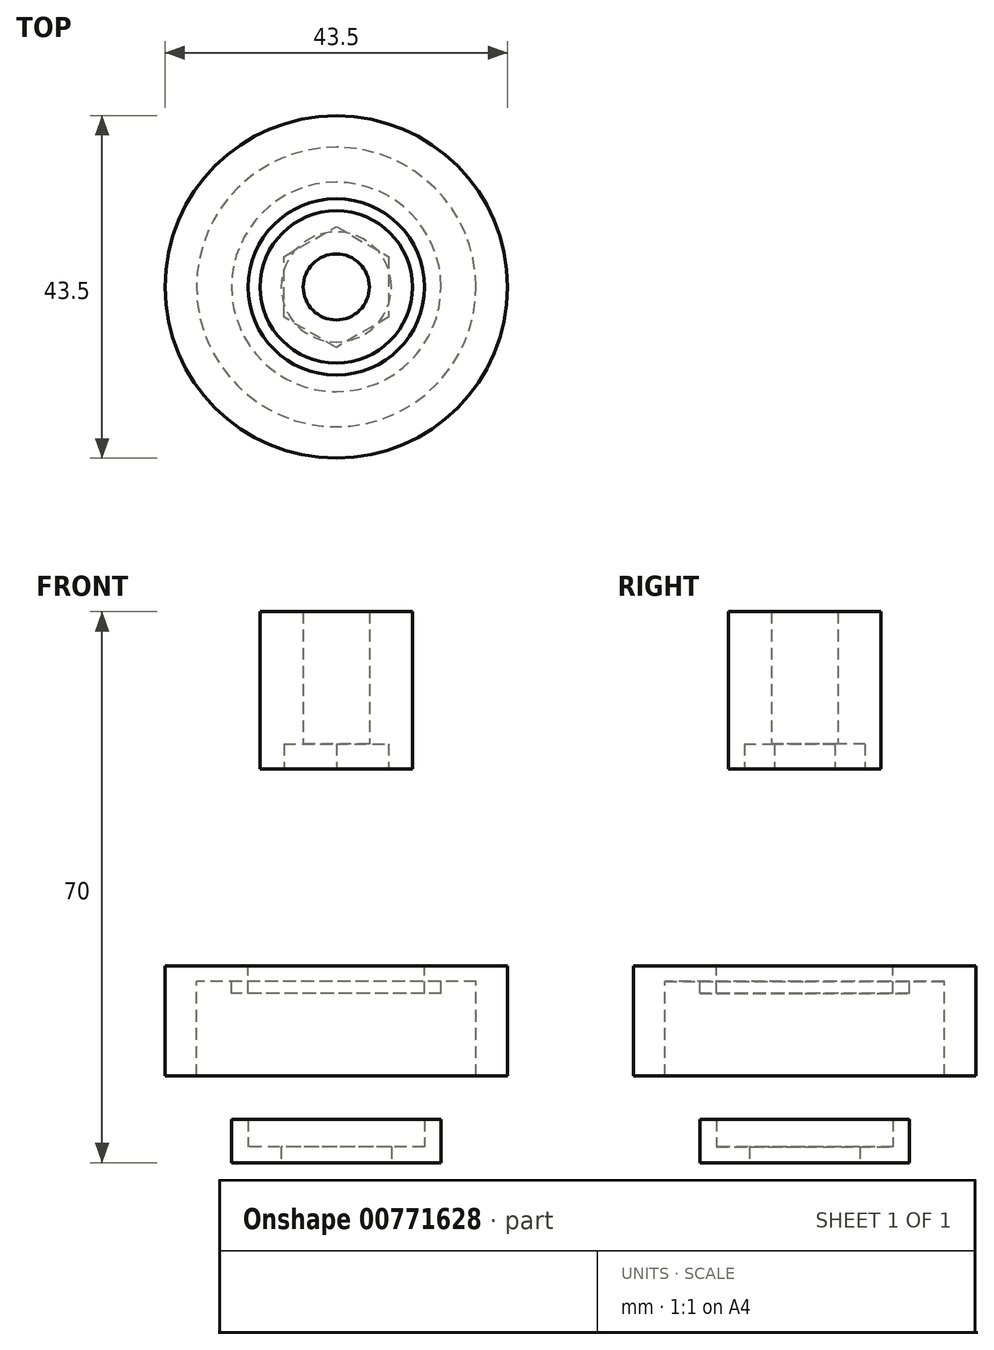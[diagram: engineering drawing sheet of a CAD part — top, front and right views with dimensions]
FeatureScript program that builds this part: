
annotation { "Feature Type Name" : "Feature", "Feature Type Description" : "" }
export const myFeature = defineFeature(function(context is Context, id is Id, definition is map)
    precondition{}
    {
        {
            assignVariable(context, id + "F0", {"variableType" : VariableType.LENGTH, "name" : "Bearing_T", "lengthValue" : 7 * mm});
        }
        {
            assignVariable(context, id + "F1", {"variableType" : VariableType.LENGTH, "name" : "Min_Wall_T", "lengthValue" : 2 * mm});
        }
        {
            assignVariable(context, id + "F2", {"variableType" : VariableType.LENGTH, "name" : "M8_Nut_T", "lengthValue" : (0.8 * 8) * mm});
        }
        {
            assignVariable(context, id + "F3", {"variableType" : VariableType.LENGTH, "name" : "Spacer_L", "lengthValue" : 20 * mm});
        }
        {
            var Q0;
            Q0=qCreatedBy(makeId("Top.planeOp"),FACE);
            var sketch = newSketch(context, id + "F4", { "sketchPlane" : qUnion([Q0])});
            skCircle(sketch, "E0", {"center": v(0, 0) * mm, "radius": 7 * mm});
            skCircle(sketch, "E1", {"center": v(0, 0) * mm, "radius": 13.3 * mm});
            skCircle(sketch, "E2", {"center": v(0, 0) * mm, "radius": 11.2 * mm});
            skSolve(sketch);
        }
        {
            var Q0;
            Q0=makeQuery(id+"F4.imprint","IMPRINT",FACE,{"disambiguationData":[TD([[makeQuery(id+"F4.imprint","IMPRINT",EDGE,{"derivedFrom":sQuery(id+"F4.wireOp",EDGE,"E0")}),-1.0]])]});
            var Q1;
            Q1=makeQuery(id+"F4.imprint","IMPRINT",FACE,{"disambiguationData":[TD([[makeQuery(id+"F4.imprint","IMPRINT",EDGE,{"derivedFrom":sQuery(id+"F4.wireOp",EDGE,"E1")}),1.0]])]});
            extrude(context, id + "F5", {"entities" : qUnion([Q0, Q1]), "depth" : getVariable(context, 'Min_Wall_T'), "offsetDistance" : 25 * mm});
        }
        {
            var Q0;
            Q0=makeQuery(id+"F4.imprint","IMPRINT",FACE,{"disambiguationData":[TD([[makeQuery(id+"F4.imprint","IMPRINT",EDGE,{"derivedFrom":sQuery(id+"F4.wireOp",EDGE,"E1")}),1.0]])]});
            extrude(context, id + "F6", {"entities" : qUnion([Q0]), "operationType" : NewBodyOperationType.ADD, "depth" : (getVariable(context, 'Bearing_T') / 2) + getVariable(context, 'Min_Wall_T'), "offsetDistance" : 25 * mm});
        }
        {
            var Q0;
            Q0=qCreatedBy(makeId("Top.planeOp"),FACE);
            cPlane(context, id + "F7", {"entities" : qUnion([Q0]), "cplaneType" : CPlaneType.OFFSET, "offset" : 25 * mm, "width" : 150 * mm, "height" : 150 * mm});
        }
        {
            var Q0;
            Q0=qCreatedBy(id+"F7.planeOp",FACE);
            var sketch = newSketch(context, id + "F8", { "sketchPlane" : qUnion([Q0])});
            skCircle(sketch, "E3", {"center": v(0, 0) * mm, "radius": 17.75 * mm});
            skCircle(sketch, "E4.0", {"center": v(0, 0) * mm, "radius": 21.75 * mm});
            skCircle(sketch, "E5.0", {"center": v(0, 0) * mm, "radius": 13.3 * mm});
            skCircle(sketch, "E6.0", {"center": v(0, 0) * mm, "radius": 11.2 * mm});
            skSolve(sketch);
        }
        {
            var Q0;
            Q0=makeQuery(id+"F8.imprint","IMPRINT",FACE,{"disambiguationData":[TD([[makeQuery(id+"F8.imprint","IMPRINT",EDGE,{"derivedFrom":sQuery(id+"F8.wireOp",EDGE,"E5.0")}),1.0]])]});
            extrude(context, id + "F9", {"entities" : qUnion([Q0]), "oppositeDirection" : true, "depth" : (getVariable(context, 'Bearing_T') / 2), "offsetDistance" : 25 * mm});
        }
        {
            var Q0;
            Q0=makeQuery(id+"F8.imprint","IMPRINT",FACE,{"disambiguationData":[TD([[makeQuery(id+"F8.imprint","IMPRINT",EDGE,{"derivedFrom":sQuery(id+"F8.wireOp",EDGE,"E3")}),1.0]])]});
            extrude(context, id + "F10", {"entities" : qUnion([Q0]), "operationType" : NewBodyOperationType.ADD, "oppositeDirection" : true, "depth" : getVariable(context, 'Min_Wall_T'), "offsetDistance" : 25 * mm});
        }
        {
            var Q0;
            Q0=qSketchRegion(id+"F8",true);
            extrude(context, id + "F11", {"entities" : qUnion([Q0]), "operationType" : NewBodyOperationType.ADD, "oppositeDirection" : true, "depth" : getVariable(context, 'Min_Wall_T') + getVariable(context, 'Bearing_T') + 5 * mm, "offsetDistance" : 25 * mm});
        }
        {
            var Q0;
            Q0=qCreatedBy(id+"F7.planeOp",FACE);
            cPlane(context, id + "F12", {"entities" : qUnion([Q0]), "cplaneType" : CPlaneType.OFFSET, "offset" : 25 * mm, "width" : 150 * mm, "height" : 150 * mm});
        }
        {
            var Q0;
            Q0=qCreatedBy(id+"F12.planeOp",FACE);
            var sketch = newSketch(context, id + "F13", { "sketchPlane" : qUnion([Q0])});
            skCircle(sketch, "E7.cCircle", {"center": v(0, 0) * mm, "radius": 6.65 * mm, "construction": true});
            skLineSegment(sketch, "E7.0", {"start": v(6.65, 3.84) * mm, "end": v(6.65, -3.84) * mm});
            skLineSegment(sketch, "E7.1", {"start": v(6.65, -3.84) * mm, "end": v(0, -7.68) * mm});
            skLineSegment(sketch, "E7.2", {"start": v(0, -7.68) * mm, "end": v(-6.65, -3.84) * mm});
            skLineSegment(sketch, "E7.3", {"start": v(-6.65, -3.84) * mm, "end": v(-6.65, 3.84) * mm});
            skLineSegment(sketch, "E7.4", {"start": v(-6.65, 3.84) * mm, "end": v(0, 7.68) * mm});
            skLineSegment(sketch, "E7.5", {"start": v(0, 7.68) * mm, "end": v(6.65, 3.84) * mm});
            skPoint(sketch, "E7.0.midPoint", {"position": v(6.65, 0) * mm});
            skCircle(sketch, "E8", {"center": v(0, 0) * mm, "radius": 9.68 * mm});
            skCircle(sketch, "E9.0", {"center": v(0, 0) * mm, "radius": 4.2 * mm});
            skSolve(sketch);
        }
        {
            var Q0;
            Q0=makeQuery(id+"F13.imprint","IMPRINT",FACE,{"disambiguationData":[TD([[makeQuery(id+"F13.imprint","IMPRINT",EDGE,{"derivedFrom":sQuery(id+"F13.wireOp",EDGE,"E7.0")}),1.0]])]});
            var Q1;
            Q1=makeQuery(id+"F13.imprint","IMPRINT",FACE,{"disambiguationData":[TD([[makeQuery(id+"F13.imprint","IMPRINT",EDGE,{"derivedFrom":sQuery(id+"F13.wireOp",EDGE,"E7.0")}),-1.0]])]});
            extrude(context, id + "F14", {"entities" : qUnion([Q0, Q1]), "depth" : getVariable(context, 'Spacer_L'), "offsetDistance" : 25 * mm});
        }
        {
            var Q0;
            Q0=makeQuery(id+"F13.imprint","IMPRINT",FACE,{"disambiguationData":[TD([[makeQuery(id+"F13.imprint","IMPRINT",EDGE,{"derivedFrom":sQuery(id+"F13.wireOp",EDGE,"E7.0")}),-1.0]])]});
            extrude(context, id + "F15", {"entities" : qUnion([Q0]), "operationType" : NewBodyOperationType.REMOVE, "depth" : getVariable(context, 'M8_Nut_T') / 2, "offsetDistance" : 25 * mm});
        }
    });
